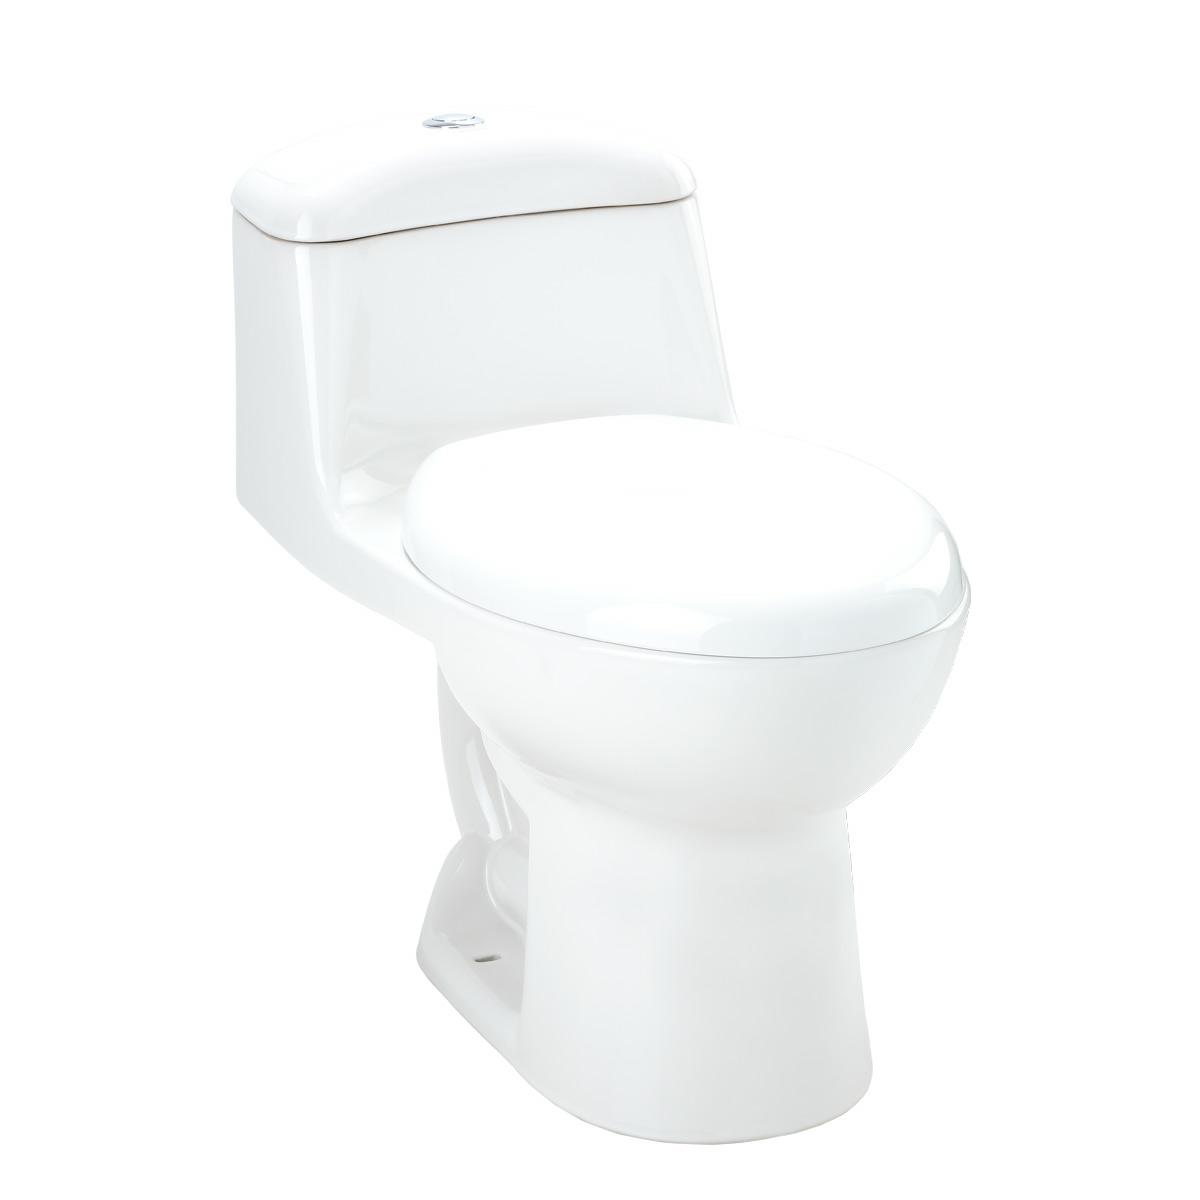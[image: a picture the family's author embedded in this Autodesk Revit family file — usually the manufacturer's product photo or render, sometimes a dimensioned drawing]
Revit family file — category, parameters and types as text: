
# Revit family: CCMX-CORONA_SMART
name_source: partatom
category: Plumbing Fixtures
units: mm (PartAtom-declared; Revit-internal decimal feet)

## family parameters
Always vertical = Yes
Cut with Voids When Loaded = No
OmniClass Number = 23.45.00.00
OmniClass Title = Sanitary, Laundry, and Cleaning Equipment
Part Type = Normal
Room Calculation Point = No
Round Connector Dimension = Use Diameter
Shared = No
Work Plane-Based = No

## types (1)
- CCMX-CORONA_SMART
    Assembly Code = D2010.60
    Consumo = Consumo de agua 4.8 litros, accionamiento de botón Single Flush.
    Description = Diseño compacto y contemporáneo que combina la eficiencia y optimización de espacio. Consumo de agua 4.8 litros, accionamiento de botón Single Flush. Capacidad de evacuación 600 gramos. Incluye asiento de cierre suave.
    Dimensiones = https://coronamexico.com
    Ficha Tecnica = https://coronamexico.com
    Garantia de Producto = 20 años en porcelana sanitaria
    Keynote = 224113
    Manufacturer = CORONA
    Model = One Piece Smart
    Type Image = ONE PIECE SMART.jpg
    URL = https://coronamexico.com

## geometry (parser evidence)
native form markers: Sweep x3
no freeform markers — native parametric forms only
